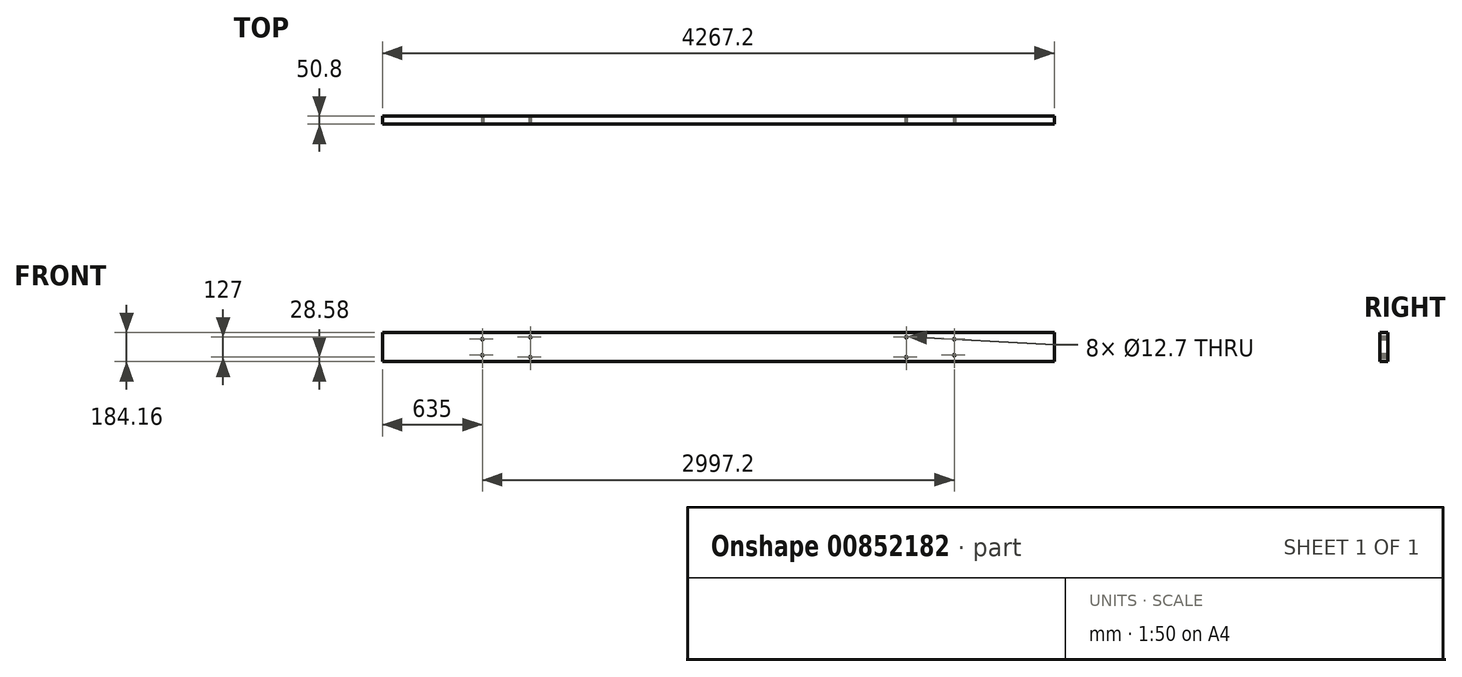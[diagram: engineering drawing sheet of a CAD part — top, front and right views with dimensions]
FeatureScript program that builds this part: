
annotation { "Feature Type Name" : "Feature", "Feature Type Description" : "" }
export const myFeature = defineFeature(function(context is Context, id is Id, definition is map)
    precondition{}
    {
        {
            var Q0;
            Q0=qCreatedBy(makeId("Front.planeOp"),FACE);
            var sketch = newSketch(context, id + "F0", { "sketchPlane" : qUnion([Q0])});
            skLineSegment(sketch, "E0.bottom", {"start": v(2133.6, -92.08) * mm, "end": v(-2133.6, -92.08) * mm});
            skLineSegment(sketch, "E0.top", {"start": v(2133.6, 92.08) * mm, "end": v(-2133.6, 92.07) * mm});
            skLineSegment(sketch, "E0.left", {"start": v(2133.6, -92.08) * mm, "end": v(2133.6, 92.08) * mm});
            skLineSegment(sketch, "E0.right", {"start": v(-2133.6, -92.08) * mm, "end": v(-2133.6, 92.07) * mm});
            skPoint(sketch, "E0.middle", {"position": v(0, 0) * mm});
            skSolve(sketch);
        }
        {
            var Q0;
            Q0 = qSketchRegion(id + "F0", true);
            extrude(context, id + "F1", {"entities" : qUnion([Q0]), "depth" : 50.8 * mm, "offsetDistance" : 25.4 * mm});
        }
        {
            var Q0;
            Q0=makeQuery(id+"F1.opExtrude","CAP_FACE",FACE,{"disambiguationData":[OSD([sQuery(id+"F0.wireOp",EDGE,"E0.bottom"),sQuery(id+"F0.wireOp",EDGE,"E0.top"),sQuery(id+"F0.wireOp",EDGE,"E0.left"),sQuery(id+"F0.wireOp",EDGE,"E0.right")])],"isStart":false});
            var sketch = newSketch(context, id + "F2", { "sketchPlane" : qUnion([Q0])});
            skLineSegment(sketch, "E1.bottom", {"start": v(1498.6, -50.8) * mm, "end": v(-1498.6, -50.8) * mm, "construction": true});
            skLineSegment(sketch, "E1.top", {"start": v(1498.6, 50.8) * mm, "end": v(-1498.6, 50.8) * mm, "construction": true});
            skLineSegment(sketch, "E1.left", {"start": v(1498.6, -50.8) * mm, "end": v(1498.6, 50.8) * mm, "construction": true});
            skLineSegment(sketch, "E1.right", {"start": v(-1498.6, -50.8) * mm, "end": v(-1498.6, 50.8) * mm, "construction": true});
            skPoint(sketch, "E1.middle", {"position": v(0, 0) * mm});
            skCircle(sketch, "E2", {"center": v(1498.6, 50.8) * mm, "radius": 6.35 * mm});
            skCircle(sketch, "E3", {"center": v(1498.6, -50.8) * mm, "radius": 6.35 * mm});
            skCircle(sketch, "E4", {"center": v(-1498.6, 50.8) * mm, "radius": 6.35 * mm});
            skCircle(sketch, "E5", {"center": v(-1498.6, -50.8) * mm, "radius": 6.35 * mm});
            skSolve(sketch);
        }
        {
            var Q0;
            Q0 = qSketchRegion(id + "F2", true);
            extrude(context, id + "F3", {"entities" : qUnion([Q0]), "operationType" : NewBodyOperationType.REMOVE, "oppositeDirection" : true, "depth" : 50.8 * mm, "offsetDistance" : 25.4 * mm});
        }
        {
            var Q0;
            Q0=qCreatedBy(makeId("Front.planeOp"),FACE);
            var sketch = newSketch(context, id + "F4", { "sketchPlane" : qUnion([Q0])});
            skLineSegment(sketch, "E6.bottom", {"start": v(1193.8, -63.5) * mm, "end": v(-1193.8, -63.5) * mm, "construction": true});
            skLineSegment(sketch, "E6.top", {"start": v(1193.8, 63.5) * mm, "end": v(-1193.8, 63.5) * mm, "construction": true});
            skLineSegment(sketch, "E6.left", {"start": v(1193.8, -63.5) * mm, "end": v(1193.8, 63.5) * mm, "construction": true});
            skLineSegment(sketch, "E6.right", {"start": v(-1193.8, -63.5) * mm, "end": v(-1193.8, 63.5) * mm, "construction": true});
            skPoint(sketch, "E6.middle", {"position": v(0, 0) * mm});
            skCircle(sketch, "E7", {"center": v(-1193.8, 63.5) * mm, "radius": 6.35 * mm});
            skCircle(sketch, "E8", {"center": v(-1193.8, -63.5) * mm, "radius": 6.35 * mm});
            skCircle(sketch, "E9", {"center": v(1193.8, 63.5) * mm, "radius": 6.35 * mm});
            skCircle(sketch, "E10", {"center": v(1193.8, -63.5) * mm, "radius": 6.35 * mm});
            skSolve(sketch);
        }
        {
            var Q0;
            Q0 = qSketchRegion(id + "F4", true);
            extrude(context, id + "F5", {"entities" : qUnion([Q0]), "operationType" : NewBodyOperationType.REMOVE, "endBound" : BoundingType.SYMMETRIC, "depth" : 101.6 * mm, "offsetDistance" : 25.4 * mm});
        }
    });
